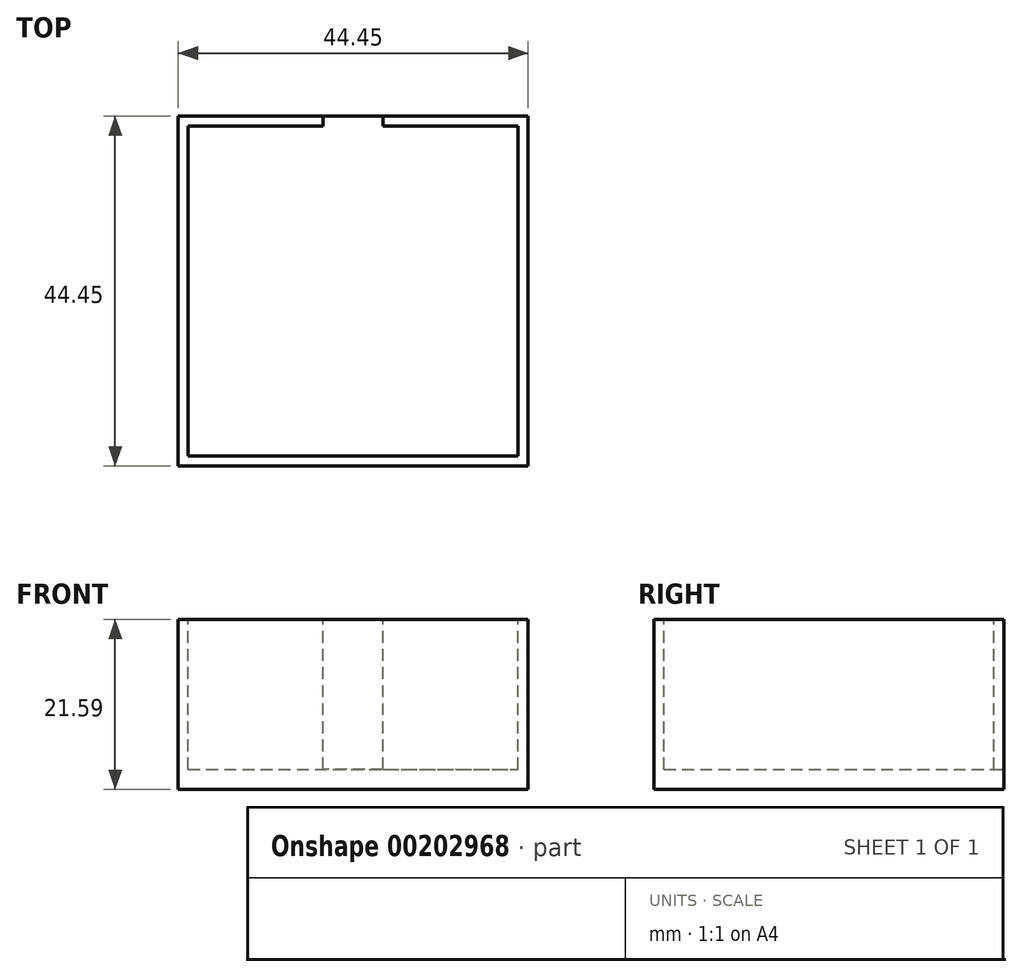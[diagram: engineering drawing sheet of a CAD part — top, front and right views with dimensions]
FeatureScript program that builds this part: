
annotation { "Feature Type Name" : "Feature", "Feature Type Description" : "" }
export const myFeature = defineFeature(function(context is Context, id is Id, definition is map)
    precondition{}
    {
        {
            var Q0;
            Q0=qCreatedBy(makeId("Top.planeOp"),FACE);
            var sketch = newSketch(context, id + "F0", { "sketchPlane" : qUnion([Q0])});
            skLineSegment(sketch, "E0.bottom", {"start": v(0, 0) * mm, "end": v(41.91, 0) * mm});
            skLineSegment(sketch, "E0.top", {"start": v(0, 41.91) * mm, "end": v(41.9, 41.91) * mm});
            skLineSegment(sketch, "E0.left", {"start": v(0, 0) * mm, "end": v(0, 41.91) * mm});
            skLineSegment(sketch, "E0.right", {"start": v(41.91, 0) * mm, "end": v(41.9, 41.91) * mm});
            skSolve(sketch);
        }
        {
            var Q0;
            Q0=makeQuery(id+"F0.imprint","IMPRINT",FACE,{"disambiguationData":[TD([[makeQuery(id+"F0.imprint","IMPRINT",EDGE,{"derivedFrom":sQuery(id+"F0.wireOp",EDGE,"E0.bottom")}),1.0]])]});
            extrude(context, id + "F1", {"entities" : qUnion([Q0]), "depth" : 2.54 * mm});
        }
        {
            var Q0;
            Q0=makeQuery(id+"F1.opExtrude","CAP_FACE",FACE,{"disambiguationData":[OSD([sQuery(id+"F0.wireOp",EDGE,"E0.bottom"),sQuery(id+"F0.wireOp",EDGE,"E0.top"),sQuery(id+"F0.wireOp",EDGE,"E0.left"),sQuery(id+"F0.wireOp",EDGE,"E0.right")])],"isStart":false});
            var sketch = newSketch(context, id + "F2", { "sketchPlane" : qUnion([Q0])});
            skLineSegment(sketch, "E1", {"start": v(0, 41.91) * mm, "end": v(20.95, 41.91) * mm});
            skLineSegment(sketch, "E2", {"start": v(20.95, 41.91) * mm, "end": v(20.95, 20.96) * mm});
            skLineSegment(sketch, "E3.bottom", {"start": v(43.18, -1.27) * mm, "end": v(-1.27, -1.27) * mm});
            skLineSegment(sketch, "E3.top", {"start": v(43.18, 43.18) * mm, "end": v(-1.27, 43.18) * mm});
            skLineSegment(sketch, "E3.left", {"start": v(43.18, -1.27) * mm, "end": v(43.18, 43.18) * mm});
            skLineSegment(sketch, "E3.right", {"start": v(-1.27, -1.27) * mm, "end": v(-1.27, 43.18) * mm});
            skPoint(sketch, "E3.middle", {"position": v(20.95, 20.96) * mm});
            skSolve(sketch);
        }
        {
            var Q0;
            {var subQ2=sQuery(id+"F2.wireOp",EDGE,"E1");Q0=makeQuery(id+"F2.imprint","IMPRINT",FACE,{"disambiguationData":[TD([[makeQuery(id+"F2.imprint","IMPRINT",EDGE,{"derivedFrom":subQ2}),1.0]])]});}
            extrude(context, id + "F3", {"entities" : qUnion([Q0]), "operationType" : NewBodyOperationType.ADD, "oppositeDirection" : true, "depth" : 2.54 * mm, "hasSecondDirection" : true, "secondDirectionOppositeDirection" : false, "secondDirectionDepth" : 19.05 * mm});
        }
        {
            var Q0;
            Q0=makeQuery(id+"F1.opExtrude","SWEPT_BODY",BODY,{"disambiguationData":[OSD([sQuery(id+"F0.wireOp",EDGE,"E0.bottom"),sQuery(id+"F0.wireOp",EDGE,"E0.top"),sQuery(id+"F0.wireOp",EDGE,"E0.left"),sQuery(id+"F0.wireOp",EDGE,"E0.right")])]});
            transform(context, id + "F4", {"entities" : qUnion([Q0]), "transformType" : TransformType.TRANSLATION_3D, "dx" : 0 * mm, "dy" : 0 * mm, "dz" : 0 * mm, "makeCopy" : true});
        }
        {
            var Q0;
            Q0=makeQuery(id+"F3.opExtrude","CAP_FACE",FACE,{"disambiguationData":[OSD([sQuery(id+"F0.wireOp",EDGE,"E0.bottom"),sQuery(id+"F0.wireOp",EDGE,"E0.top"),sQuery(id+"F0.wireOp",EDGE,"E0.left"),sQuery(id+"F0.wireOp",EDGE,"E0.right"),sQuery(id+"F2.wireOp",EDGE,"E1"),sQuery(id+"F2.wireOp",EDGE,"E3.bottom"),sQuery(id+"F2.wireOp",EDGE,"E3.top"),sQuery(id+"F2.wireOp",EDGE,"E3.left"),sQuery(id+"F2.wireOp",EDGE,"E3.right")])],"isStart":true});
            var sketch = newSketch(context, id + "F5", { "sketchPlane" : qUnion([Q0])});
            skLineSegment(sketch, "E4", {"start": v(-1.27, 43.18) * mm, "end": v(17.14, 43.18) * mm});
            skLineSegment(sketch, "E5", {"start": v(17.14, 43.18) * mm, "end": v(17.14, 41.91) * mm});
            skLineSegment(sketch, "E6", {"start": v(17.14, 41.91) * mm, "end": v(24.77, 41.91) * mm});
            skLineSegment(sketch, "E7", {"start": v(24.77, 41.91) * mm, "end": v(24.77, 43.18) * mm});
            skLineSegment(sketch, "E8", {"start": v(24.77, 43.18) * mm, "end": v(17.14, 43.18) * mm});
            skSolve(sketch);
        }
        {
            var Q0;
            Q0 = qSketchRegion(id + "F5", true);
            extrude(context, id + "F6", {"entities" : qUnion([Q0]), "operationType" : NewBodyOperationType.REMOVE, "oppositeDirection" : true, "depth" : 19.05 * mm});
        }
        {
            var Q0;
            Q0=makeQuery(id+"F4.opPattern","COPY",BODY,{"derivedFrom":makeQuery(id+"F1.opExtrude","SWEPT_BODY",BODY,{"disambiguationData":[OSD([sQuery(id+"F0.wireOp",EDGE,"E0.bottom"),sQuery(id+"F0.wireOp",EDGE,"E0.top"),sQuery(id+"F0.wireOp",EDGE,"E0.left"),sQuery(id+"F0.wireOp",EDGE,"E0.right")])]}),"instanceName":"1"});
            deleteBodies(context, id + "F7", {"entities" : qUnion([Q0])});
        }
    });
